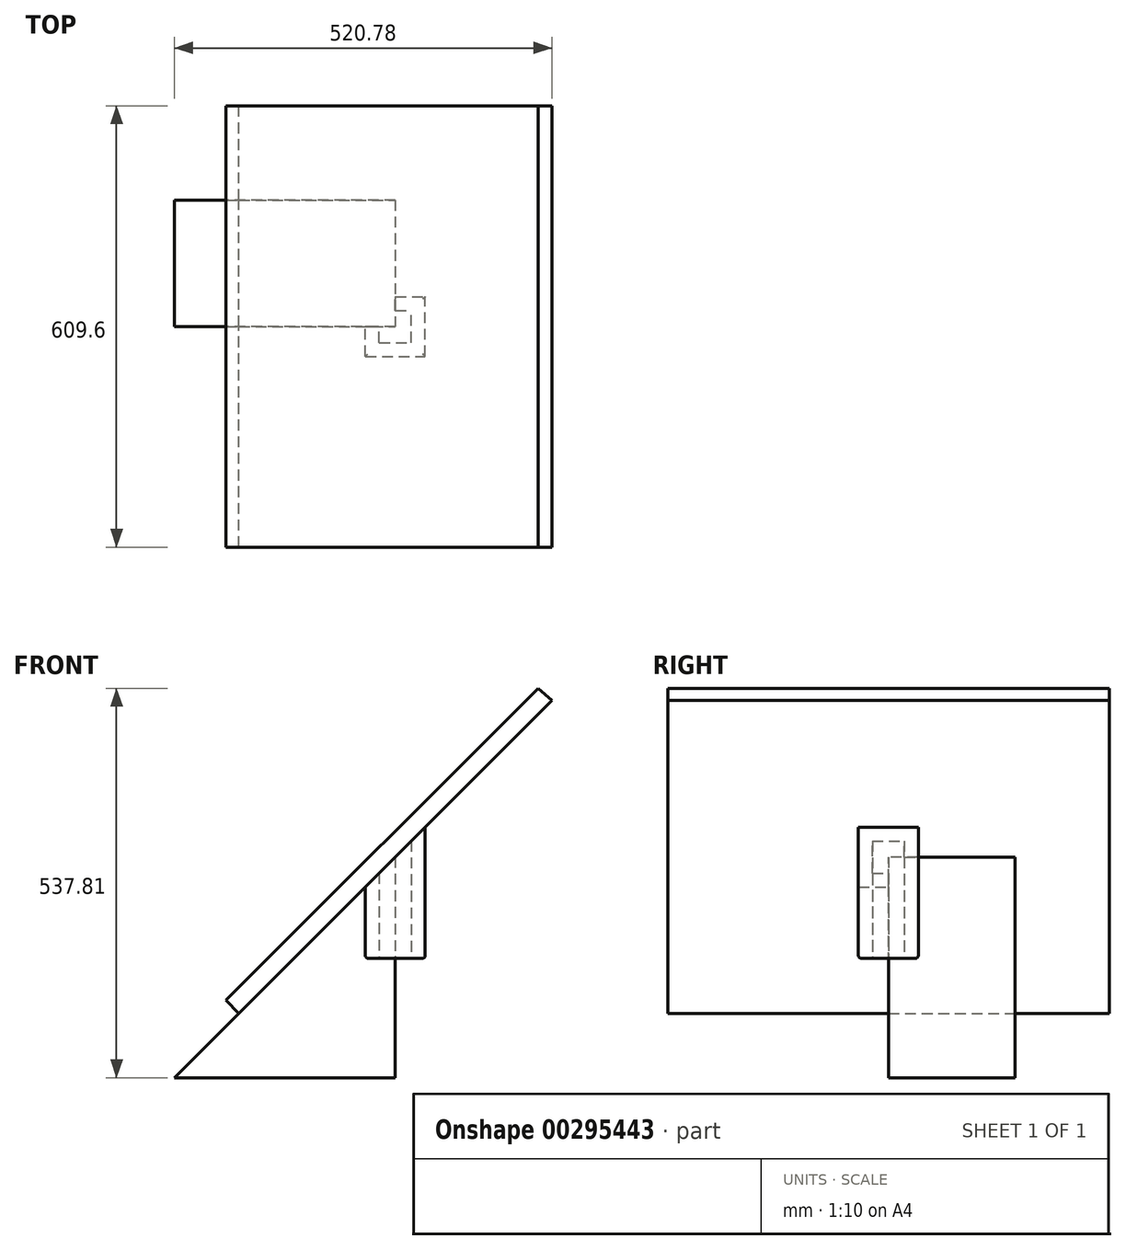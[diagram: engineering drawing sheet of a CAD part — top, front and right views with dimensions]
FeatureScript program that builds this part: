
annotation { "Feature Type Name" : "Feature", "Feature Type Description" : "" }
export const myFeature = defineFeature(function(context is Context, id is Id, definition is map)
    precondition{}
    {
        {
            var Q0;
            Q0=qCreatedBy(makeId("Front.planeOp"),FACE);
            var sketch = newSketch(context, id + "F0", { "sketchPlane" : qUnion([Q0])});
            skLineSegment(sketch, "E0", {"start": v(-215.98, -215.98) * mm, "end": v(215.98, 215.98) * mm});
            skLineSegment(sketch, "E1", {"start": v(-215.98, -215.98) * mm, "end": v(-233.94, -198.02) * mm});
            skLineSegment(sketch, "E2", {"start": v(-233.94, -198.02) * mm, "end": v(197.13, 233) * mm});
            skLineSegment(sketch, "E3", {"start": v(197.13, 233) * mm, "end": v(215.98, 215.98) * mm});
            skSolve(sketch);
        }
        {
            var Q0;
            Q0 = qSketchRegion(id + "F0", true);
            extrude(context, id + "F1", {"entities" : qUnion([Q0]), "endBound" : BoundingType.SYMMETRIC, "depth" : 609.6 * mm});
        }
        {
            var Q0;
            Q0=qCreatedBy(makeId("Front.planeOp"),FACE);
            var sketch = newSketch(context, id + "F2", { "sketchPlane" : qUnion([Q0])});
            skLineSegment(sketch, "E4", {"start": v(0, 0) * mm, "end": v(0, -304.8) * mm});
            skLineSegment(sketch, "E5", {"start": v(0, -304.8) * mm, "end": v(-304.8, -304.8) * mm});
            skLineSegment(sketch, "E6", {"start": v(-304.8, -304.8) * mm, "end": v(0, 0) * mm});
            skSolve(sketch);
        }
        {
            var Q0;
            Q0 = qSketchRegion(id + "F2", true);
            extrude(context, id + "F3", {"entities" : qUnion([Q0]), "operationType" : NewBodyOperationType.ADD, "oppositeDirection" : true, "depth" : 174.62 * mm});
        }
        {
            var Q0;
            Q0=qCreatedBy(makeId("Top.planeOp"),FACE);
            var sketch = newSketch(context, id + "F4", { "sketchPlane" : qUnion([Q0])});
            skLineSegment(sketch, "E7.bottom", {"start": v(-41.28, -41.28) * mm, "end": v(0, -41.28) * mm});
            skLineSegment(sketch, "E7.top", {"start": v(0, 41.28) * mm, "end": v(41.27, 41.28) * mm});
            skLineSegment(sketch, "E7.left", {"start": v(-41.28, -41.28) * mm, "end": v(-41.28, 0) * mm});
            skLineSegment(sketch, "E7.right", {"start": v(41.28, -41.28) * mm, "end": v(41.27, 0) * mm});
            skLineSegment(sketch, "E8", {"start": v(41.27, 0) * mm, "end": v(41.27, 41.28) * mm});
            skLineSegment(sketch, "E9", {"start": v(0, -41.28) * mm, "end": v(41.28, -41.28) * mm});
            skLineSegment(sketch, "E10.bottom", {"start": v(-22.23, -22.23) * mm, "end": v(22.22, -22.23) * mm});
            skLineSegment(sketch, "E10.top", {"start": v(0, 22.23) * mm, "end": v(22.22, 22.23) * mm});
            skLineSegment(sketch, "E10.left", {"start": v(-22.23, -22.23) * mm, "end": v(-22.23, 0) * mm});
            skLineSegment(sketch, "E10.right", {"start": v(22.22, -22.23) * mm, "end": v(22.22, 22.23) * mm});
            skLineSegment(sketch, "E11", {"start": v(-41.28, 0) * mm, "end": v(-22.23, 0) * mm});
            skLineSegment(sketch, "E12", {"start": v(0, 22.23) * mm, "end": v(0, 41.28) * mm});
            skSolve(sketch);
        }
        {
            var Q0;
            Q0 = qSketchRegion(id + "F4", true);
            var Q1;
            Q1=makeQuery(id+"F1.opExtrude","SWEPT_FACE",FACE,{"disambiguationData":[OSD([sQuery(id+"F0.wireOp",EDGE,"E0")])]});
            extrude(context, id + "F5", {"entities" : qUnion([Q0]), "endBound" : BoundingType.UP_TO_SURFACE, "endBoundEntityFace" : qUnion([Q1]), "depth" : 152.4 * mm, "hasSecondDirection" : true, "secondDirectionOppositeDirection" : true, "secondDirectionDepth" : 139.7 * mm});
        }
        {
            var Q0;
            Q0=makeQuery(id+"F5.opExtrude","CAP_EDGE",EDGE,{"disambiguationData":[OSD([sQuery(id+"F4.wireOp",EDGE,"E7.right"),sQuery(id+"F4.wireOp",EDGE,"E8")])],"isStart":true});
            var Q1;
            Q1=makeQuery(id+"F5.opExtrude","CAP_EDGE",EDGE,{"disambiguationData":[OSD([sQuery(id+"F4.wireOp",EDGE,"E7.bottom"),sQuery(id+"F4.wireOp",EDGE,"E9")])],"isStart":true});
            var Q2;
            Q2=makeQuery(id+"F5.opExtrude","CAP_EDGE",EDGE,{"disambiguationData":[OSD([sQuery(id+"F4.wireOp",EDGE,"E7.top")])],"isStart":true});
            var Q3;
            Q3=makeQuery(id+"F5.opExtrude","CAP_EDGE",EDGE,{"disambiguationData":[OSD([sQuery(id+"F4.wireOp",EDGE,"E7.left")])],"isStart":true});
            fillet(context, id + "F6", {"entities" : qUnion([Q0, Q1, Q2, Q3]), "radius" : 3.17 * mm, "tangentPropagation" : true, "allowEdgeOverflow" : false});
        }
    });
